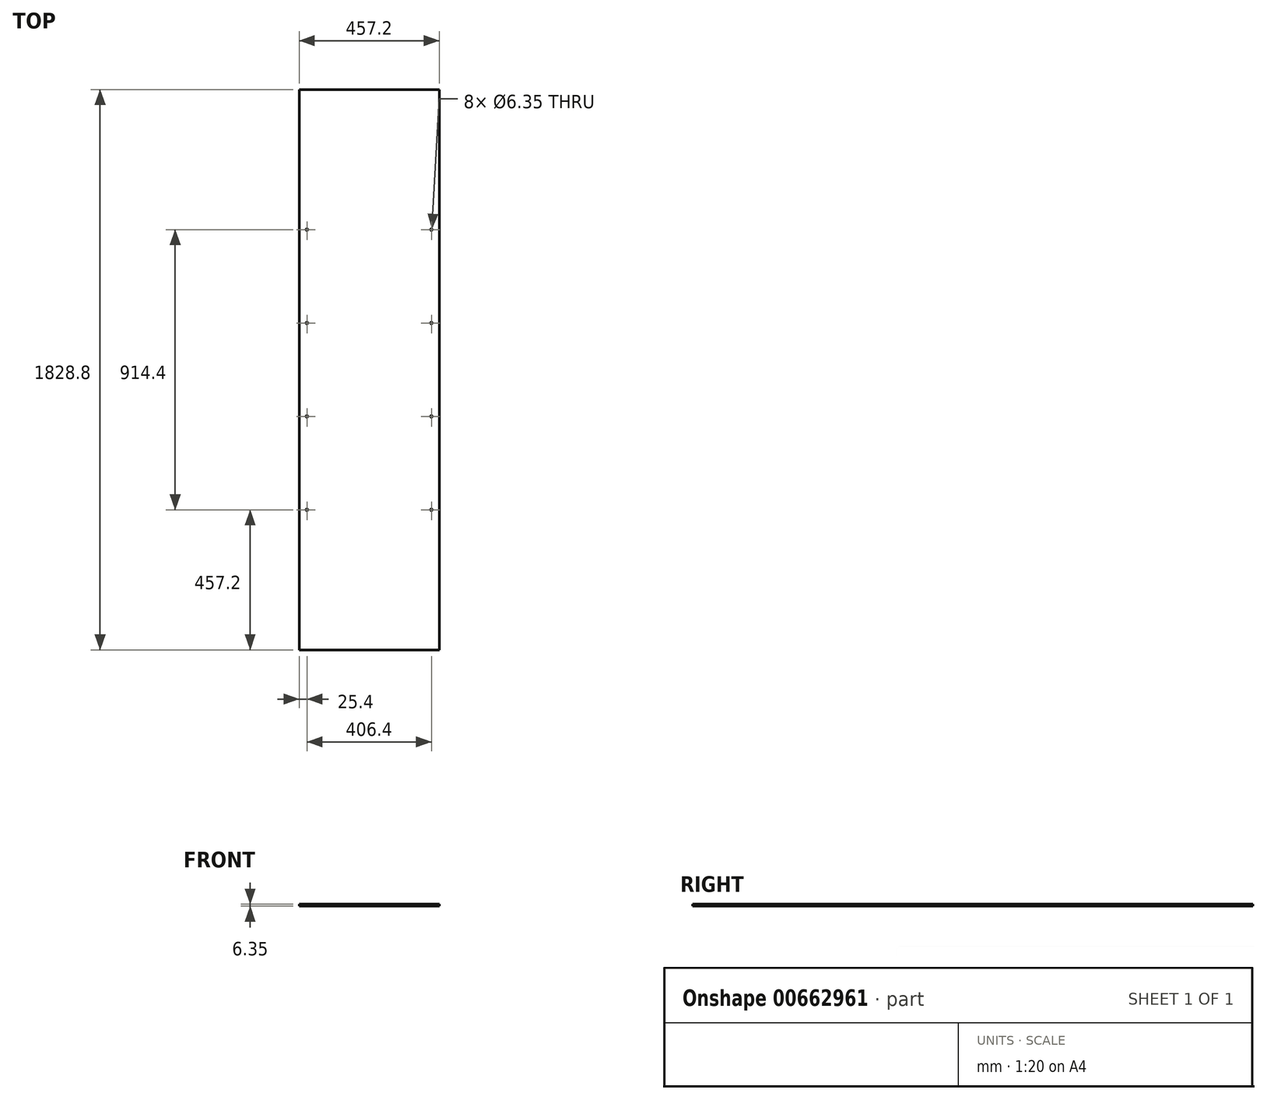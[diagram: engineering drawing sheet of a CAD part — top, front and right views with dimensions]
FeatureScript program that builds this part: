
annotation { "Feature Type Name" : "Feature", "Feature Type Description" : "" }
export const myFeature = defineFeature(function(context is Context, id is Id, definition is map)
    precondition{}
    {
        {
            var Q0;
            Q0=qCreatedBy(makeId("Top.planeOp"),FACE);
            var sketch = newSketch(context, id + "F0", { "sketchPlane" : qUnion([Q0])});
            skLineSegment(sketch, "E0.bottom", {"start": v(228.6, 914.4) * mm, "end": v(-228.6, 914.4) * mm});
            skLineSegment(sketch, "E0.top", {"start": v(228.6, -914.4) * mm, "end": v(-228.6, -914.4) * mm});
            skLineSegment(sketch, "E0.left", {"start": v(228.6, 914.4) * mm, "end": v(228.6, -914.4) * mm});
            skLineSegment(sketch, "E0.right", {"start": v(-228.6, 914.4) * mm, "end": v(-228.6, -914.4) * mm});
            skPoint(sketch, "E0.middle", {"position": v(0, 0) * mm});
            skSolve(sketch);
        }
        {
            var Q0;
            Q0 = qSketchRegion(id + "F0", true);
            extrude(context, id + "F1", {"entities" : qUnion([Q0]), "depth" : 6.35 * mm, "offsetDistance" : 25.4 * mm});
        }
        {
            var Q0;
            Q0=makeQuery(id+"F1.opExtrude","CAP_FACE",FACE,{"disambiguationData":[OSD([sQuery(id+"F0.wireOp",EDGE,"E0.bottom"),sQuery(id+"F0.wireOp",EDGE,"E0.top"),sQuery(id+"F0.wireOp",EDGE,"E0.left"),sQuery(id+"F0.wireOp",EDGE,"E0.right")])],"isStart":false});
            var sketch = newSketch(context, id + "F2", { "sketchPlane" : qUnion([Q0])});
            skLineSegment(sketch, "E1", {"start": v(228.6, 863.6) * mm, "end": v(-228.6, 863.6) * mm});
            skLineSegment(sketch, "E2", {"start": v(228.6, -863.6) * mm, "end": v(-228.6, -863.6) * mm});
            skSolve(sketch);
        }
        {
            var Q0;
            {var subQ0=sQuery(id+"F2.wireOp",EDGE,"E1");Q0=makeQuery(id+"F2.imprint","IMPRINT",FACE,{"disambiguationData":[TD([[makeQuery(id+"F2.imprint","IMPRINT",EDGE,{"derivedFrom":subQ0}),1.0]])]});}
            var sketch = newSketch(context, id + "F3", { "sketchPlane" : qUnion([Q0])});
            skLineSegment(sketch, "E3", {"start": v(0, 0) * mm, "end": v(-203.2, 0) * mm, "construction": true});
            skLineSegment(sketch, "E4", {"start": v(0, 0) * mm, "end": v(203.2, 0) * mm, "construction": true});
            skCircle(sketch, "E5", {"center": v(-203.2, 152.4) * mm, "radius": 3.17 * mm});
            skCircle(sketch, "E6", {"center": v(-203.2, -152.4) * mm, "radius": 3.17 * mm});
            skCircle(sketch, "E7", {"center": v(-203.2, -457.2) * mm, "radius": 3.18 * mm});
            skCircle(sketch, "E8", {"center": v(203.2, 152.4) * mm, "radius": 3.17 * mm});
            skCircle(sketch, "E9", {"center": v(203.2, 457.2) * mm, "radius": 3.17 * mm});
            skCircle(sketch, "E10", {"center": v(203.2, -152.4) * mm, "radius": 3.17 * mm});
            skCircle(sketch, "E11", {"center": v(203.2, -457.2) * mm, "radius": 3.17 * mm});
            skCircle(sketch, "E12", {"center": v(-203.2, 457.2) * mm, "radius": 3.17 * mm});
            skSolve(sketch);
        }
        {
            var Q0;
            Q0 = qSketchRegion(id + "F3", true);
            extrude(context, id + "F4", {"entities" : qUnion([Q0]), "operationType" : NewBodyOperationType.REMOVE, "oppositeDirection" : true, "depth" : 25.4 * mm, "offsetDistance" : 25.4 * mm});
        }
    });
